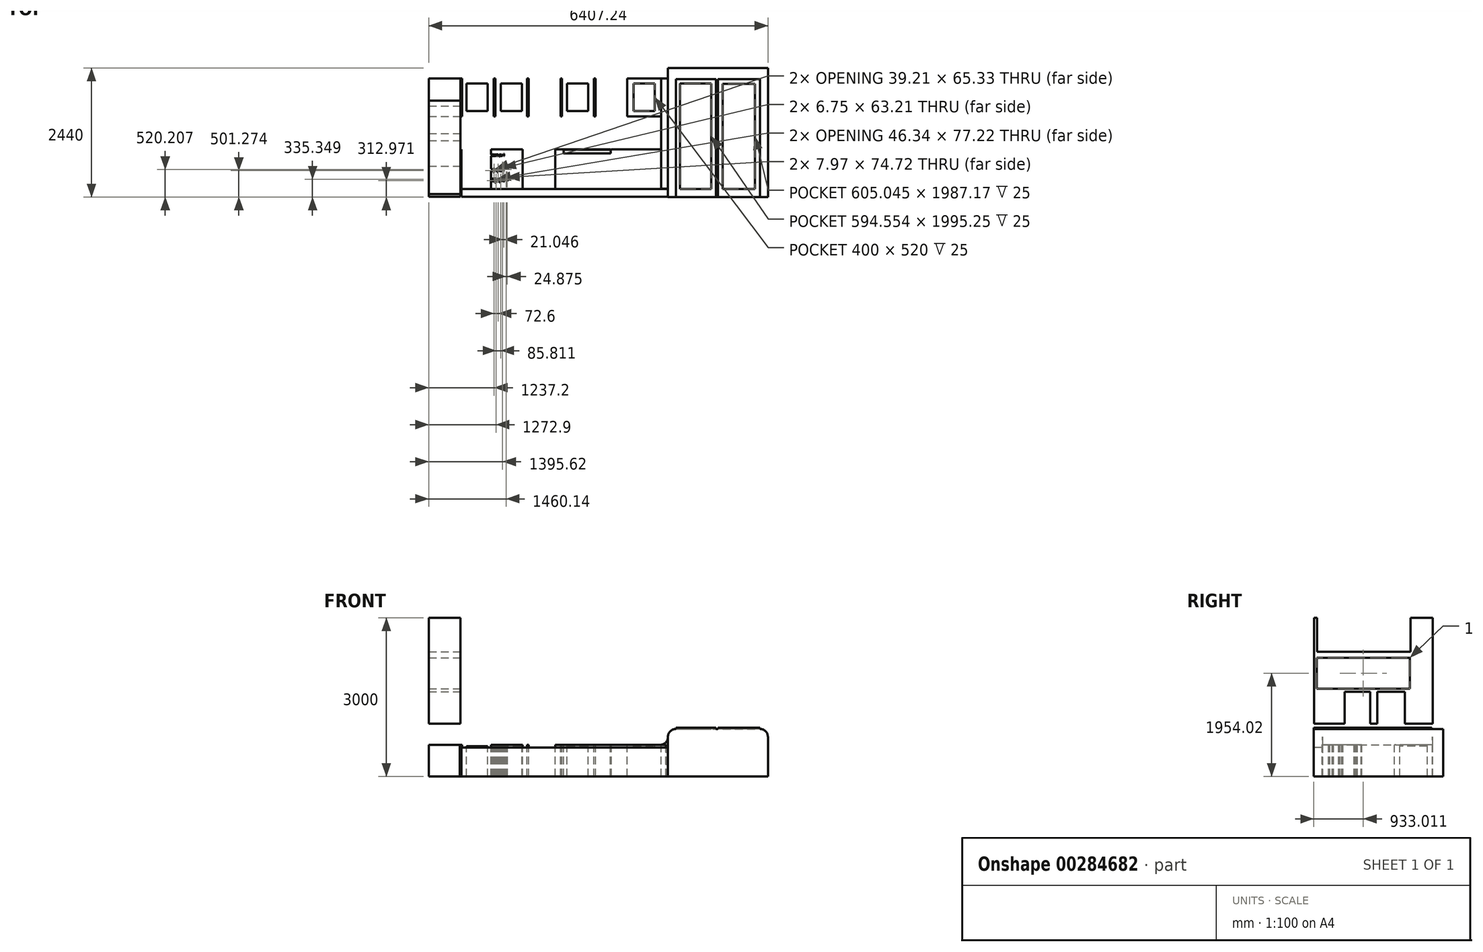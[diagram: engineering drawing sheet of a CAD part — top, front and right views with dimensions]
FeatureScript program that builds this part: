
annotation { "Feature Type Name" : "Feature", "Feature Type Description" : "" }
export const myFeature = defineFeature(function(context is Context, id is Id, definition is map)
    precondition{}
    {
        {
            var Q0;
            Q0=qCreatedBy(makeId("Top.planeOp"), FACE);
            var sketch = newSketch(context, id + "F0", { "sketchPlane" : qUnion([Q0])});
            skLineSegment(sketch, "E0.bottom", {"start": v(0, 750) * mm, "end": v(1806, 750) * mm});
            skLineSegment(sketch, "E0.top", {"start": v(0, 0) * mm, "end": v(3890, 0) * mm});
            skLineSegment(sketch, "E0.left", {"start": v(0, 750) * mm, "end": v(0, 0) * mm});
            skLineSegment(sketch, "E0.right", {"start": v(3890, 750) * mm, "end": v(3890, 0) * mm});
            skLineSegment(sketch, "E1.bottom", {"start": v(1190, 750) * mm, "end": v(1790, 750) * mm});
            skLineSegment(sketch, "E1.top", {"start": v(1190, 0) * mm, "end": v(1790, 0) * mm});
            skLineSegment(sketch, "E1.left", {"start": v(1190, 750) * mm, "end": v(1190, 0) * mm});
            skLineSegment(sketch, "E1.right", {"start": v(1790, 750) * mm, "end": v(1790, 0) * mm});
            skLineSegment(sketch, "E2.bottom", {"start": v(600, 740) * mm, "end": v(1164, 740) * mm});
            skLineSegment(sketch, "E2.top", {"start": v(600, 590) * mm, "end": v(1164, 590) * mm});
            skLineSegment(sketch, "E2.left", {"start": v(600, 740) * mm, "end": v(600, 590) * mm});
            skLineSegment(sketch, "E2.right", {"start": v(1164, 740) * mm, "end": v(1164, 590) * mm});
            skLineSegment(sketch, "E3.bottom", {"start": v(600, 560) * mm, "end": v(1164, 560) * mm});
            skLineSegment(sketch, "E3.top", {"start": v(600, 300) * mm, "end": v(1164, 300) * mm});
            skLineSegment(sketch, "E3.left", {"start": v(600, 560) * mm, "end": v(600, 300) * mm});
            skLineSegment(sketch, "E3.right", {"start": v(1164, 560) * mm, "end": v(1164, 300) * mm});
            skLineSegment(sketch, "E4.bottom", {"start": v(600, 270) * mm, "end": v(1164, 270) * mm});
            skLineSegment(sketch, "E4.top", {"start": v(600, 10) * mm, "end": v(1164, 10) * mm});
            skLineSegment(sketch, "E4.left", {"start": v(600, 270) * mm, "end": v(600, 10) * mm});
            skLineSegment(sketch, "E4.right", {"start": v(1164, 270) * mm, "end": v(1164, 10) * mm});
            skLineSegment(sketch, "E5.top", {"start": v(1816, 590) * mm, "end": v(2843, 590) * mm});
            skLineSegment(sketch, "E5.left", {"start": v(1816, 740) * mm, "end": v(1816, 590) * mm});
            skLineSegment(sketch, "E5.right", {"start": v(2843, 740) * mm, "end": v(2843, 590) * mm});
            skLineSegment(sketch, "E6.top", {"start": v(1816, 300) * mm, "end": v(2843, 300) * mm});
            skLineSegment(sketch, "E6.right", {"start": v(2843, 750) * mm, "end": v(2843, 590) * mm});
            skLineSegment(sketch, "E7.bottom", {"start": v(1826, 270) * mm, "end": v(2843, 270) * mm});
            skLineSegment(sketch, "E7.top", {"start": v(1826, 10) * mm, "end": v(2843, 10) * mm});
            skLineSegment(sketch, "E7.left", {"start": v(1826, 270) * mm, "end": v(1826, 10) * mm});
            skLineSegment(sketch, "E7.right", {"start": v(2843, 270) * mm, "end": v(2843, 10) * mm});
            skLineSegment(sketch, "E8.bottom", {"start": v(2853, 740) * mm, "end": v(3880, 740) * mm});
            skLineSegment(sketch, "E8.top", {"start": v(2853, 590) * mm, "end": v(3880, 590) * mm});
            skLineSegment(sketch, "E8.left", {"start": v(2853, 740) * mm, "end": v(2853, 590) * mm});
            skLineSegment(sketch, "E9.bottom", {"start": v(2853, 560) * mm, "end": v(3880, 560) * mm});
            skLineSegment(sketch, "E9.top", {"start": v(2853, 300) * mm, "end": v(3880, 300) * mm});
            skLineSegment(sketch, "E9.left", {"start": v(2853, 560) * mm, "end": v(2853, 300) * mm});
            skLineSegment(sketch, "E9.right", {"start": v(3880, 560) * mm, "end": v(3880, 300) * mm});
            skLineSegment(sketch, "E10.bottom", {"start": v(2853, 270) * mm, "end": v(3880, 270) * mm});
            skLineSegment(sketch, "E10.top", {"start": v(2853, 10) * mm, "end": v(3880, 10) * mm});
            skLineSegment(sketch, "E10.left", {"start": v(2853, 270) * mm, "end": v(2853, 10) * mm});
            skLineSegment(sketch, "E10.right", {"start": v(3880, 270) * mm, "end": v(3880, 10) * mm});
            skLineSegment(sketch, "E11.bottom", {"start": v(12.85, 1370) * mm, "end": v(3902.85, 1370) * mm});
            skLineSegment(sketch, "E11.top", {"start": v(12.85, 2090) * mm, "end": v(3902.85, 2090) * mm});
            skLineSegment(sketch, "E11.left", {"start": v(12.85, 1370) * mm, "end": v(12.85, 2090) * mm});
            skLineSegment(sketch, "E11.right", {"start": v(3902.85, 1370) * mm, "end": v(3902.85, 2090) * mm});
            skText(sketch, "E12", { "text": "Dishwasher", "fontName": "OpenSans-Regular.ttf"});
            skLineSegment(sketch, "E13", {"start": v(1174, 750) * mm, "end": v(1174, 0) * mm});
            skLineSegment(sketch, "E14", {"start": v(1806, 750) * mm, "end": v(1806, 0) * mm});
            skLineSegment(sketch, "E15", {"start": v(1816, 740) * mm, "end": v(2843, 740) * mm});
            skLineSegment(sketch, "E16", {"start": v(3890, 750) * mm, "end": v(1806, 750) * mm});
            skLineSegment(sketch, "E17", {"start": v(3880, 590) * mm, "end": v(3880, 740) * mm});
            skLineSegment(sketch, "E18", {"start": v(1816, 300) * mm, "end": v(1816, 560) * mm});
            skLineSegment(sketch, "E19", {"start": v(1816, 560) * mm, "end": v(2843, 560) * mm});
            skLineSegment(sketch, "E20.trimOffspring", {"start": v(2843, 560) * mm, "end": v(2843, 300) * mm});
            skLineSegment(sketch, "E21.bottom", {"start": v(42.85, 2090) * mm, "end": v(642.85, 2090) * mm});
            skLineSegment(sketch, "E21.top", {"start": v(42.85, 1370) * mm, "end": v(642.85, 1370) * mm});
            skLineSegment(sketch, "E21.left", {"start": v(42.85, 2090) * mm, "end": v(42.85, 1370) * mm});
            skLineSegment(sketch, "E21.right", {"start": v(642.85, 2090) * mm, "end": v(642.85, 1370) * mm});
            skLineSegment(sketch, "E22", {"start": v(6000, -150) * mm, "end": v(6000, 2090) * mm, "construction": true});
            skPoint(sketch, "E23", {"position": v(6000, 0) * mm});
            skPoint(sketch, "E24", {"position": v(6000, 1370) * mm});
            skPoint(sketch, "E25", {"position": v(6000, 750) * mm});
            skPoint(sketch, "E26", {"position": v(6000, 770) * mm});
            skLineSegment(sketch, "E27", {"start": v(6000, 2090) * mm, "end": v(5702.85, 2090) * mm, "construction": true});
            skLineSegment(sketch, "E28", {"start": v(6000, 2090) * mm, "end": v(6000, 2090) * mm});
            skLineSegment(sketch, "E29.bottom", {"start": v(672.85, 2090) * mm, "end": v(1272.85, 2090) * mm});
            skLineSegment(sketch, "E29.top", {"start": v(672.85, 1370) * mm, "end": v(1272.85, 1370) * mm});
            skLineSegment(sketch, "E29.left", {"start": v(672.85, 2090) * mm, "end": v(672.85, 1370) * mm});
            skLineSegment(sketch, "E29.right", {"start": v(1272.85, 2090) * mm, "end": v(1272.85, 1370) * mm});
            skLineSegment(sketch, "E30.bottom", {"start": v(1302.85, 2090) * mm, "end": v(1902.85, 2090) * mm});
            skLineSegment(sketch, "E30.top", {"start": v(1302.85, 1370) * mm, "end": v(1902.85, 1370) * mm});
            skLineSegment(sketch, "E30.left", {"start": v(1302.85, 2090) * mm, "end": v(1302.85, 1370) * mm});
            skLineSegment(sketch, "E30.right", {"start": v(1902.85, 2090) * mm, "end": v(1902.85, 1370) * mm});
            skLineSegment(sketch, "E31.bottom", {"start": v(1932.85, 2090) * mm, "end": v(2532.85, 2090) * mm});
            skLineSegment(sketch, "E31.top", {"start": v(1932.85, 1370) * mm, "end": v(2532.85, 1370) * mm});
            skLineSegment(sketch, "E31.left", {"start": v(1932.85, 2090) * mm, "end": v(1932.85, 1370) * mm});
            skLineSegment(sketch, "E31.right", {"start": v(2532.85, 2090) * mm, "end": v(2532.85, 1370) * mm});
            skLineSegment(sketch, "E32.bottom", {"start": v(2562.85, 2090) * mm, "end": v(3162.85, 2090) * mm});
            skLineSegment(sketch, "E32.top", {"start": v(2562.85, 1370) * mm, "end": v(3162.85, 1370) * mm});
            skLineSegment(sketch, "E32.left", {"start": v(2562.85, 2090) * mm, "end": v(2562.85, 1370) * mm});
            skLineSegment(sketch, "E32.right", {"start": v(3162.85, 2090) * mm, "end": v(3162.85, 1370) * mm});
            skLineSegment(sketch, "E33.bottom", {"start": v(3162.85, 2090) * mm, "end": v(3192.85, 2090) * mm});
            skLineSegment(sketch, "E33.top", {"start": v(3162.85, 1370) * mm, "end": v(3192.85, 1370) * mm});
            skLineSegment(sketch, "E33.left", {"start": v(3192.85, 2090) * mm, "end": v(3192.85, 1370) * mm});
            skLineSegment(sketch, "E34.bottom", {"start": v(3192.85, 2090) * mm, "end": v(3792.85, 2090) * mm});
            skLineSegment(sketch, "E34.top", {"start": v(3192.85, 1370) * mm, "end": v(3792.85, 1370) * mm});
            skLineSegment(sketch, "E34.right", {"start": v(3792.85, 2090) * mm, "end": v(3792.85, 1370) * mm});
            skLineSegment(sketch, "E35.bottom", {"start": v(30, 750) * mm, "end": v(590, 750) * mm});
            skLineSegment(sketch, "E35.top", {"start": v(30, 0) * mm, "end": v(590, 0) * mm});
            skLineSegment(sketch, "E35.left", {"start": v(30, 750) * mm, "end": v(30, 0) * mm});
            skLineSegment(sketch, "E35.right", {"start": v(590, 750) * mm, "end": v(590, 0) * mm});
            skText(sketch, "E36", { "text": "Lemans II \n541.32.620", "fontName": "OpenSans-Regular.ttf"});
            skText(sketch, "E37", { "text": "Bottom pull", "fontName": "OpenSans-Regular.ttf"});
            skText(sketch, "E38", { "text": "top pull", "fontName": "OpenSans-Regular.ttf"});
            skText(sketch, "E39", { "text": "top pull", "fontName": "OpenSans-Regular.ttf"});
            skLineSegment(sketch, "E40", {"start": v(6000, -150) * mm, "end": v(0, -150) * mm, "construction": true});
            skLineSegment(sketch, "E41.bottom", {"start": v(3902.85, 2090) * mm, "end": v(5702.85, 2090) * mm});
            skLineSegment(sketch, "E41.top", {"start": v(3902.85, 0) * mm, "end": v(5702.85, 0) * mm});
            skLineSegment(sketch, "E41.left", {"start": v(3902.85, 2090) * mm, "end": v(3902.85, 0) * mm});
            skLineSegment(sketch, "E41.right", {"start": v(5702.85, 2090) * mm, "end": v(5702.85, 0) * mm});
            skLineSegment(sketch, "E42", {"start": v(4772.85, 2090) * mm, "end": v(4772.85, 0) * mm});
            skLineSegment(sketch, "E43", {"start": v(4802.85, 2090) * mm, "end": v(4802.85, 0) * mm});
            skLineSegment(sketch, "E44", {"start": v(3932.85, 2090) * mm, "end": v(3932.85, 0) * mm});
            skLineSegment(sketch, "E45.bottom", {"start": v(127.34, 1990) * mm, "end": v(527.34, 1990) * mm});
            skLineSegment(sketch, "E45.top", {"start": v(127.34, 1470) * mm, "end": v(527.34, 1470) * mm});
            skLineSegment(sketch, "E45.left", {"start": v(127.34, 1990) * mm, "end": v(127.34, 1470) * mm});
            skLineSegment(sketch, "E45.right", {"start": v(527.34, 1990) * mm, "end": v(527.34, 1470) * mm});
            skLineSegment(sketch, "E46.bottom", {"start": v(772.85, 1990) * mm, "end": v(1172.85, 1990) * mm});
            skLineSegment(sketch, "E46.top", {"start": v(772.85, 1470) * mm, "end": v(1172.85, 1470) * mm});
            skLineSegment(sketch, "E46.left", {"start": v(772.85, 1990) * mm, "end": v(772.85, 1470) * mm});
            skLineSegment(sketch, "E46.right", {"start": v(1172.85, 1990) * mm, "end": v(1172.85, 1470) * mm});
            skLineSegment(sketch, "E47.bottom", {"start": v(2028.05, 1990) * mm, "end": v(2428.05, 1990) * mm});
            skLineSegment(sketch, "E47.top", {"start": v(2028.05, 1470) * mm, "end": v(2428.05, 1470) * mm});
            skLineSegment(sketch, "E47.left", {"start": v(2028.05, 1990) * mm, "end": v(2028.05, 1470) * mm});
            skLineSegment(sketch, "E47.right", {"start": v(2428.05, 1990) * mm, "end": v(2428.05, 1470) * mm});
            skLineSegment(sketch, "E48.bottom", {"start": v(3280.66, 1990) * mm, "end": v(3680.66, 1990) * mm});
            skLineSegment(sketch, "E48.top", {"start": v(3280.66, 1470) * mm, "end": v(3680.66, 1470) * mm});
            skLineSegment(sketch, "E48.left", {"start": v(3280.66, 1990) * mm, "end": v(3280.66, 1470) * mm});
            skLineSegment(sketch, "E48.right", {"start": v(3680.66, 1990) * mm, "end": v(3680.66, 1470) * mm});
            skText(sketch, "E49", { "text": "Stove", "fontName": "OpenSans-Regular.ttf"});
            skPoint(sketch, "E50", {"position": v(2061.13, 1179.17) * mm});
            skPoint(sketch, "E51", {"position": v(2414.2, 750) * mm});
            skLineSegment(sketch, "E52.bottom", {"start": v(1964.2, 750) * mm, "end": v(2864.2, 750) * mm});
            skLineSegment(sketch, "E52.top", {"start": v(1964.2, 670) * mm, "end": v(2864.2, 670) * mm});
            skLineSegment(sketch, "E52.left", {"start": v(1964.2, 750) * mm, "end": v(1964.2, 670) * mm});
            skLineSegment(sketch, "E52.right", {"start": v(2864.2, 750) * mm, "end": v(2864.2, 670) * mm});
            skLineSegment(sketch, "E53.bottom", {"start": v(3932.85, 2090) * mm, "end": v(4091.6, 2090) * mm});
            skLineSegment(sketch, "E53.top", {"start": v(3932.85, -150) * mm, "end": v(4091.6, -150) * mm});
            skLineSegment(sketch, "E53.left", {"start": v(3932.85, 2090) * mm, "end": v(3932.85, -150) * mm});
            skLineSegment(sketch, "E53.right", {"start": v(4091.6, 2090) * mm, "end": v(4091.6, -150) * mm});
            skLineSegment(sketch, "E54.bottom", {"start": v(5586.52, 2090) * mm, "end": v(5820.09, 2090) * mm});
            skLineSegment(sketch, "E54.top", {"start": v(5586.52, -159.02) * mm, "end": v(5820.09, -159.02) * mm});
            skLineSegment(sketch, "E54.left", {"start": v(5586.52, 2090) * mm, "end": v(5586.52, -159.02) * mm});
            skLineSegment(sketch, "E54.right", {"start": v(5820.09, 2090) * mm, "end": v(5820.09, -159.02) * mm});
            skPoint(sketch, "E55.oppositeSnap0", {"position": v(5703.3, 2090) * mm});
            skLineSegment(sketch, "E55.bottom", {"start": v(3932.85, 2286.83) * mm, "end": v(5820.09, 2286.83) * mm});
            skLineSegment(sketch, "E55.top", {"start": v(3932.85, 2090) * mm, "end": v(5820.09, 2090) * mm});
            skLineSegment(sketch, "E55.left", {"start": v(3932.85, 2286.83) * mm, "end": v(3932.85, 2090) * mm});
            skLineSegment(sketch, "E55.right", {"start": v(5820.09, 2286.83) * mm, "end": v(5820.09, 2090) * mm});
            skLineSegment(sketch, "E56.trimOffspring", {"start": v(3932.85, 2090) * mm, "end": v(12.85, 2090) * mm, "construction": true});
            skLineSegment(sketch, "E57.trimOffspring", {"start": v(5586.52, 2090) * mm, "end": v(4091.6, 2090) * mm, "construction": true});
            skLineSegment(sketch, "E58.bottom", {"start": v(1405.73, 1990) * mm, "end": v(1817.16, 1990) * mm});
            skLineSegment(sketch, "E58.top", {"start": v(1405.73, 1470) * mm, "end": v(1817.16, 1470) * mm});
            skLineSegment(sketch, "E58.left", {"start": v(1405.73, 1990) * mm, "end": v(1405.73, 1470) * mm});
            skLineSegment(sketch, "E58.right", {"start": v(1817.16, 1990) * mm, "end": v(1817.16, 1470) * mm});
            skLineSegment(sketch, "E59.bottom", {"start": v(2646, 1990) * mm, "end": v(3066.6, 1990) * mm});
            skLineSegment(sketch, "E59.top", {"start": v(2646, 1470) * mm, "end": v(3066.6, 1470) * mm});
            skLineSegment(sketch, "E59.left", {"start": v(2646, 1990) * mm, "end": v(2646, 1470) * mm});
            skLineSegment(sketch, "E59.right", {"start": v(3066.6, 1990) * mm, "end": v(3066.6, 1470) * mm});
            skLineSegment(sketch, "E60.bottom", {"start": v(30, 0) * mm, "end": v(0, 0) * mm});
            skLineSegment(sketch, "E60.top", {"start": v(30, -150) * mm, "end": v(0, -150) * mm});
            skLineSegment(sketch, "E60.left", {"start": v(30, 0) * mm, "end": v(30, -150) * mm});
            skLineSegment(sketch, "E60.right", {"start": v(0, 0) * mm, "end": v(0, -150) * mm});
            skLineSegment(sketch, "E61.bottom", {"start": v(0, 0) * mm, "end": v(3932.85, 0) * mm});
            skLineSegment(sketch, "E61.top", {"start": v(0, -150) * mm, "end": v(3932.85, -150) * mm});
            skLineSegment(sketch, "E61.right", {"start": v(3932.85, 0) * mm, "end": v(3932.85, -150) * mm});
            skLineSegment(sketch, "E62.bottom", {"start": v(4091.6, 0) * mm, "end": v(5586.52, 0) * mm});
            skLineSegment(sketch, "E62.top", {"start": v(4091.6, -159.02) * mm, "end": v(5586.52, -159.02) * mm});
            skLineSegment(sketch, "E62.left", {"start": v(4091.6, 0) * mm, "end": v(4091.6, -159.02) * mm});
            skLineSegment(sketch, "E62.right", {"start": v(5586.52, 0) * mm, "end": v(5586.52, -159.02) * mm});
            const initialGuessF0  = {"E12": [1.29, 0.4978, 1, 0, 0.0522], "E36": [0.08, 0.61298, 1, 0, 0.04765], "E37": [0.54096, 0.62134, 1, 0, 0.03929], "E38": [0.54368, 0.33543, 1, 0, 0.0599], "E39": [0.56002, 0.14482, 1, 0, 0.0708], "E49": [1.91777, 1.09917, 1, 0, 0.08]};
            skSetInitialGuess(sketch, initialGuessF0);
            skSolve(sketch);
        }
        {
            var Q0;
            {var subQ0=sQuery(id+"F0.wireOp",EDGE,"E11.left");Q0=makeQuery(id+"F0.imprint","IMPRINT",FACE,{"disambiguationData":[TD([[makeQuery(id+"F0.imprint","IMPRINT",EDGE,{"derivedFrom":subQ0}),-1.0]])]});}
            var Q1;
            Q1=makeQuery(id+"F0.imprint","IMPRINT",FACE,{"disambiguationData":[TD([[makeQuery(id+"F0.imprint","IMPRINT",EDGE,{"derivedFrom":sQuery(id+"F0.wireOp",EDGE,"E21.bottom")}),-1.0]])]});
            var Q2;
            {var subQ0=sQuery(id+"F0.wireOp",EDGE,"E21.right");Q2=makeQuery(id+"F0.imprint","IMPRINT",FACE,{"disambiguationData":[TD([[makeQuery(id+"F0.imprint","IMPRINT",EDGE,{"derivedFrom":subQ0}),1.0]])]});}
            var Q3;
            Q3=makeQuery(id+"F0.imprint","IMPRINT",FACE,{"disambiguationData":[TD([[makeQuery(id+"F0.imprint","IMPRINT",EDGE,{"derivedFrom":sQuery(id+"F0.wireOp",EDGE,"E29.bottom")}),-1.0]])]});
            var Q4;
            Q4=makeQuery(id+"F0.imprint","IMPRINT",FACE,{"disambiguationData":[TD([[makeQuery(id+"F0.imprint","IMPRINT",EDGE,{"derivedFrom":sQuery(id+"F0.wireOp",EDGE,"E30.bottom")}),-1.0]])]});
            var Q5;
            Q5=makeQuery(id+"F0.imprint","IMPRINT",FACE,{"disambiguationData":[TD([[makeQuery(id+"F0.imprint","IMPRINT",EDGE,{"derivedFrom":sQuery(id+"F0.wireOp",EDGE,"E32.bottom")}),-1.0]])]});
            var Q6;
            {var subQ0=sQuery(id+"F0.wireOp",EDGE,"E31.right");Q6=makeQuery(id+"F0.imprint","IMPRINT",FACE,{"disambiguationData":[TD([[makeQuery(id+"F0.imprint","IMPRINT",EDGE,{"derivedFrom":subQ0}),1.0]])]});}
            var Q7;
            Q7=makeQuery(id+"F0.imprint","IMPRINT",FACE,{"disambiguationData":[TD([[makeQuery(id+"F0.imprint","IMPRINT",EDGE,{"derivedFrom":sQuery(id+"F0.wireOp",EDGE,"E32.right")}),1.0]])]});
            var Q8;
            Q8=makeQuery(id+"F0.imprint","IMPRINT",FACE,{"disambiguationData":[TD([[makeQuery(id+"F0.imprint","IMPRINT",EDGE,{"derivedFrom":sQuery(id+"F0.wireOp",EDGE,"E33.left")}),1.0]])]});
            var Q9;
            Q9=makeQuery(id+"F0.imprint","IMPRINT",FACE,{"disambiguationData":[TD([[makeQuery(id+"F0.imprint","IMPRINT",EDGE,{"derivedFrom":sQuery(id+"F0.wireOp",EDGE,"E48.bottom")}),-1.0]])]});
            var Q10;
            {var subQ3=sQuery(id+"F0.wireOp",EDGE,"E34.right");Q10=makeQuery(id+"F0.imprint","IMPRINT",FACE,{"disambiguationData":[TD([[makeQuery(id+"F0.imprint","IMPRINT",EDGE,{"derivedFrom":subQ3}),1.0]])]});}
            var Q11;
            {var subQ4=sQuery(id+"F0.wireOp",EDGE,"E41.bottom");Q11=makeQuery(id+"F0.imprint","IMPRINT",FACE,{"disambiguationData":[TD([[makeQuery(id+"F0.imprint","IMPRINT",EDGE,{"derivedFrom":subQ4}),-1.0]])]});}
            var Q12;
            {var subQ0=sQuery(id+"F0.wireOp",EDGE,"E53.left");var subQ1=sQuery(id+"F0.wireOp",EDGE,"E41.top");var subQ2=makeQuery(id+"F0.imprint","INTERSECT",VERTEX,{"derivedFrom":[subQ1,subQ0]});Q12=makeQuery(id+"F0.imprint","IMPRINT",FACE,{"disambiguationData":[TD([[makeQuery(id+"F0.imprint","IMPRINT",EDGE,{"disambiguationData":[TD([[subQ2,-1.0]])],"derivedFrom":subQ1}),1.0]])]});}
            var Q13;
            Q13=makeQuery(id+"F0.imprint","IMPRINT",FACE,{"disambiguationData":[TD([[makeQuery(id+"F0.imprint","IMPRINT",EDGE,{"derivedFrom":sQuery(id+"F0.wireOp",EDGE,"E55.bottom")}),-1.0]])]});
            var Q14;
            {var subQ0=sQuery(id+"F0.wireOp",EDGE,"E42");Q14=makeQuery(id+"F0.imprint","IMPRINT",FACE,{"disambiguationData":[TD([[makeQuery(id+"F0.imprint","IMPRINT",EDGE,{"derivedFrom":subQ0}),-1.0]])]});}
            var Q15;
            {var subQ0=sQuery(id+"F0.wireOp",EDGE,"E42");Q15=makeQuery(id+"F0.imprint","IMPRINT",FACE,{"disambiguationData":[TD([[makeQuery(id+"F0.imprint","IMPRINT",EDGE,{"derivedFrom":subQ0}),1.0]])]});}
            var Q16;
            Q16=makeQuery(id+"F0.imprint","IMPRINT",FACE,{"disambiguationData":[TD([[makeQuery(id+"F0.imprint","IMPRINT",EDGE,{"derivedFrom":sQuery(id+"F0.wireOp",EDGE,"E1.bottom")}),-1.0]])]});
            var Q17;
            {var subQ7=sQuery(id+"F0.wireOp",EDGE,"E5.top");Q17=makeQuery(id+"F0.imprint","IMPRINT",FACE,{"disambiguationData":[TD([[makeQuery(id+"F0.imprint","IMPRINT",EDGE,{"derivedFrom":subQ7}),1.0]])]});}
            var Q18;
            {var subQ0=sQuery(id+"F0.wireOp",EDGE,"E42");Q18=makeQuery(id+"F0.imprint","IMPRINT",FACE,{"disambiguationData":[TD([[makeQuery(id+"F0.imprint","IMPRINT",EDGE,{"derivedFrom":subQ0}),-1.0]])]});}
            var Q19;
            {var subQ0=sQuery(id+"F0.wireOp",EDGE,"E41.right");Q19=makeQuery(id+"F0.imprint","IMPRINT",FACE,{"disambiguationData":[TD([[makeQuery(id+"F0.imprint","IMPRINT",EDGE,{"derivedFrom":subQ0}),-1.0]])]});}
            var Q20;
            {var subQ0=sQuery(id+"F0.wireOp",EDGE,"E43");Q20=makeQuery(id+"F0.imprint","IMPRINT",FACE,{"disambiguationData":[TD([[makeQuery(id+"F0.imprint","IMPRINT",EDGE,{"derivedFrom":subQ0}),1.0]])]});}
            var Q21;
            {var subQ4=sQuery(id+"F0.wireOp",EDGE,"E41.right");Q21=makeQuery(id+"F0.imprint","IMPRINT",FACE,{"disambiguationData":[TD([[makeQuery(id+"F0.imprint","IMPRINT",EDGE,{"derivedFrom":subQ4}),1.0]])]});}
            var Q22;
            {var subQ1=sQuery(id+"F0.wireOp",EDGE,"E8.top");Q22=makeQuery(id+"F0.imprint","IMPRINT",FACE,{"disambiguationData":[TD([[makeQuery(id+"F0.imprint","IMPRINT",EDGE,{"derivedFrom":subQ1}),1.0]])]});}
            var Q23;
            Q23=makeQuery(id+"F0.imprint","IMPRINT",FACE,{"disambiguationData":[TD([[makeQuery(id+"F0.imprint","IMPRINT",EDGE,{"derivedFrom":sQuery(id+"F0.wireOp",EDGE,"E9.bottom")}),-1.0]])]});
            var Q24;
            Q24=makeQuery(id+"F0.imprint","IMPRINT",FACE,{"disambiguationData":[TD([[makeQuery(id+"F0.imprint","IMPRINT",EDGE,{"derivedFrom":sQuery(id+"F0.wireOp",EDGE,"E10.bottom")}),-1.0]])]});
            var Q25;
            Q25=makeQuery(id+"F0.imprint","IMPRINT",FACE,{"disambiguationData":[TD([[makeQuery(id+"F0.imprint","IMPRINT",EDGE,{"derivedFrom":sQuery(id+"F0.wireOp",EDGE,"E7.bottom")}),-1.0]])]});
            var Q26;
            Q26=makeQuery(id+"F0.imprint","IMPRINT",FACE,{"disambiguationData":[TD([[makeQuery(id+"F0.imprint","IMPRINT",EDGE,{"derivedFrom":sQuery(id+"F0.wireOp",EDGE,"E6.top")}),1.0]])]});
            var Q27;
            {var subQ0=sQuery(id+"F0.wireOp",EDGE,"E15");var subQ1=sQuery(id+"F0.wireOp",EDGE,"E6.right");var subQ2=makeQuery(id+"F0.imprint","INTERSECT",VERTEX,{"derivedFrom":[subQ1,subQ0]});Q27=makeQuery(id+"F0.imprint","IMPRINT",FACE,{"disambiguationData":[TD([[makeQuery(id+"F0.imprint","IMPRINT",EDGE,{"disambiguationData":[TD([[subQ2,-1.0]])],"derivedFrom":subQ1}),-1.0]])]});}
            var Q28;
            {var subQ7=sQuery(id+"F0.wireOp",EDGE,"E3.bottom");Q28=makeQuery(id+"F0.imprint","IMPRINT",FACE,{"disambiguationData":[TD([[makeQuery(id+"F0.imprint","IMPRINT",EDGE,{"derivedFrom":subQ7}),-1.0]])]});}
            var Q29;
            {var subQ8=sQuery(id+"F0.wireOp",EDGE,"E2.bottom");Q29=makeQuery(id+"F0.imprint","IMPRINT",FACE,{"disambiguationData":[TD([[makeQuery(id+"F0.imprint","IMPRINT",EDGE,{"derivedFrom":subQ8}),-1.0]])]});}
            var Q30;
            Q30=makeQuery(id+"F0.imprint","IMPRINT",FACE,{"disambiguationData":[TD([[makeQuery(id+"F0.imprint","IMPRINT",EDGE,{"derivedFrom":sQuery(id+"F0.wireOp",EDGE,"E4.bottom")}),-1.0]])]});
            var Q31;
            {var subQ14=sQuery(id+"F0.wireOp",EDGE,"E35.bottom");Q31=makeQuery(id+"F0.imprint","IMPRINT",FACE,{"disambiguationData":[TD([[makeQuery(id+"F0.imprint","IMPRINT",EDGE,{"derivedFrom":subQ14}),-1.0]])]});}
            var Q32;
            {var subQ0=sQuery(id+"F0.wireOp",EDGE,"E0.left");Q32=makeQuery(id+"F0.imprint","IMPRINT",FACE,{"disambiguationData":[TD([[makeQuery(id+"F0.imprint","IMPRINT",EDGE,{"derivedFrom":subQ0}),1.0]])]});}
            var Q33;
            Q33=makeQuery(id+"F0.imprint","IMPRINT",FACE,{"disambiguationData":[TD([[makeQuery(id+"F0.imprint","IMPRINT",EDGE,{"derivedFrom":sQuery(id+"F0.wireOp",EDGE,"E45.bottom")}),-1.0]])]});
            var Q34;
            Q34=makeQuery(id+"F0.imprint","IMPRINT",FACE,{"disambiguationData":[TD([[makeQuery(id+"F0.imprint","IMPRINT",EDGE,{"derivedFrom":sQuery(id+"F0.wireOp",EDGE,"E46.bottom")}),-1.0]])]});
            var Q35;
            Q35=makeQuery(id+"F0.imprint","IMPRINT",FACE,{"disambiguationData":[TD([[makeQuery(id+"F0.imprint","IMPRINT",EDGE,{"derivedFrom":sQuery(id+"F0.wireOp",EDGE,"E31.bottom")}),-1.0]])]});
            var Q36;
            Q36=makeQuery(id+"F0.imprint","IMPRINT",FACE,{"disambiguationData":[TD([[makeQuery(id+"F0.imprint","IMPRINT",EDGE,{"derivedFrom":sQuery(id+"F0.wireOp",EDGE,"E47.bottom")}),-1.0]])]});
            var Q37;
            {var subQ5=sQuery(id+"F0.wireOp",EDGE,"E53.top");Q37=makeQuery(id+"F0.imprint","IMPRINT",FACE,{"disambiguationData":[TD([[makeQuery(id+"F0.imprint","IMPRINT",EDGE,{"derivedFrom":subQ5}),1.0]])]});}
            var Q38;
            {var subQ0=sQuery(id+"F0.wireOp",EDGE,"E29.right");Q38=makeQuery(id+"F0.imprint","IMPRINT",FACE,{"disambiguationData":[TD([[makeQuery(id+"F0.imprint","IMPRINT",EDGE,{"derivedFrom":subQ0}),1.0]])]});}
            var Q39;
            {var subQ0=sQuery(id+"F0.wireOp",EDGE,"E30.right");Q39=makeQuery(id+"F0.imprint","IMPRINT",FACE,{"disambiguationData":[TD([[makeQuery(id+"F0.imprint","IMPRINT",EDGE,{"derivedFrom":subQ0}),1.0]])]});}
            var Q40;
            {var subQ0=sQuery(id+"F0.wireOp",EDGE,"E0.right");Q40=makeQuery(id+"F0.imprint","IMPRINT",FACE,{"disambiguationData":[TD([[makeQuery(id+"F0.imprint","IMPRINT",EDGE,{"derivedFrom":subQ0}),-1.0]])]});}
            var Q41;
            {var subQ0=sQuery(id+"F0.wireOp",EDGE,"E8.left");var subQ1=sQuery(id+"F0.wireOp",EDGE,"E8.bottom");var subQ2=makeQuery(id+"F0.imprint","INTERSECT",VERTEX,{"derivedFrom":[subQ1,subQ0]});Q41=makeQuery(id+"F0.imprint","IMPRINT",FACE,{"disambiguationData":[TD([[makeQuery(id+"F0.imprint","IMPRINT",EDGE,{"disambiguationData":[TD([[subQ2,-1.0]])],"derivedFrom":subQ1}),-1.0]])]});}
            var Q42;
            {var subQ0=sQuery(id+"F0.wireOp",EDGE,"E1.left");Q42=makeQuery(id+"F0.imprint","IMPRINT",FACE,{"disambiguationData":[TD([[makeQuery(id+"F0.imprint","IMPRINT",EDGE,{"derivedFrom":subQ0}),-1.0]])]});}
            var Q43;
            {var subQ30=sQuery(id+"F0.wireOp",EDGE,"E2.bottom");Q43=makeQuery(id+"F0.imprint","IMPRINT",FACE,{"disambiguationData":[TD([[makeQuery(id+"F0.imprint","IMPRINT",EDGE,{"derivedFrom":subQ30}),1.0]])]});}
            extrude(context, id + "F1", {"entities" : qUnion([Q0, Q1, Q2, Q3, Q4, Q5, Q6, Q7, Q8, Q9, Q10, Q11, Q12, Q13, Q14, Q15, Q16, Q17, Q18, Q19, Q20, Q21, Q22, Q23, Q24, Q25, Q26, Q27, Q28, Q29, Q30, Q31, Q32, Q33, Q34, Q35, Q36, Q37, Q38, Q39, Q40, Q41, Q42, Q43]), "oppositeDirection" : true, "depth" : 600 * mm});
        }
        {
            var Q0;
            Q0=makeQuery(id+"F1.opExtrude","SWEPT_FACE",FACE,{"disambiguationData":[OSD([sQuery(id+"F0.wireOp",EDGE,"E55.bottom")])]});
            var sketch = newSketch(context, id + "F2", { "sketchPlane" : qUnion([Q0])});
            skLineSegment(sketch, "E63.bottom", {"start": v(-3932.85, -600) * mm, "end": v(-5820.09, -600) * mm});
            skLineSegment(sketch, "E63.top", {"start": v(-4082.85, 300) * mm, "end": v(-5670.09, 300) * mm});
            skLineSegment(sketch, "E63.left", {"start": v(-3932.85, 150) * mm, "end": v(-3932.85, 150) * mm});
            skLineSegment(sketch, "E63.right", {"start": v(-5820.09, -600) * mm, "end": v(-5820.09, 150) * mm});
            skPoint(sketch, "E64.visualSharp", {"position": v(-3932.85, 300) * mm});
            skArc(sketch, "E64.filletArc", {"start": v(-3932.85, 150) * mm, "mid": v(-3976.78, 256.07) * mm, "end": v(-4082.85, 300) * mm});
            skPoint(sketch, "E65.visualSharp", {"position": v(-5820.09, 300) * mm});
            skArc(sketch, "E65.filletArc", {"start": v(-5670.09, 300) * mm, "mid": v(-5776.15, 256.07) * mm, "end": v(-5820.09, 150) * mm});
            skPoint(sketch, "E66.visualSharp", {"position": v(-3932.85, 0) * mm});
            skLineSegment(sketch, "E67.bottom", {"start": v(-3932.85, -600) * mm, "end": v(-3803.33, -600) * mm});
            skLineSegment(sketch, "E67.left", {"start": v(-3932.85, -600) * mm, "end": v(-3932.85, 150) * mm});
            skLineSegment(sketch, "E67.right", {"start": v(-3803.33, -600) * mm, "end": v(-3803.33, 1.4) * mm});
            skLineSegment(sketch, "E68", {"start": v(-3782.85, 0) * mm, "end": v(-3782.85, 0) * mm});
            skArc(sketch, "E69.filletArc", {"start": v(-3932.85, 150) * mm, "mid": v(-3895.92, 51.44) * mm, "end": v(-3803.33, 1.4) * mm});
            skPoint(sketch, "E67.top.end.orphan", {"position": v(-3803.33, 150) * mm});
            skPoint(sketch, "E70.bottom.start.orphan", {"position": v(-3766.85, 0) * mm});
            skSolve(sketch);
        }
        {
            var Q0;
            Q0=makeQuery(id+"F2.imprint","IMPRINT",FACE,{"disambiguationData":[TD([[makeQuery(id+"F2.imprint","IMPRINT",EDGE,{"derivedFrom":sQuery(id+"F2.wireOp",EDGE,"E63.top")}),1.0]])]});
            var Q1;
            {var subQ0=sQuery(id+"F2.wireOp",EDGE,"E63.bottom");Q1=makeQuery(id+"F2.imprint","IMPRINT",FACE,{"disambiguationData":[TD([[makeQuery(id+"F2.imprint","IMPRINT",EDGE,{"derivedFrom":subQ0}),-1.0]])]});}
            extrude(context, id + "F3", {"entities" : qUnion([Q0, Q1]), "operationType" : NewBodyOperationType.ADD, "oppositeDirection" : true, "depth" : 2440 * mm});
        }
        {
            var Q0;
            Q0=makeQuery(id+"F3.opExtrude","SWEPT_FACE",FACE,{"disambiguationData":[OSD([sQuery(id+"F2.wireOp",EDGE,"E63.top")])]});
            var sketch = newSketch(context, id + "F4", { "sketchPlane" : qUnion([Q0])});
            skLineSegment(sketch, "E71.bottom", {"start": v(4082.85, 2073.08) * mm, "end": v(4839.76, 2073.08) * mm});
            skLineSegment(sketch, "E71.top", {"start": v(4082.85, -153.17) * mm, "end": v(4839.76, -153.17) * mm});
            skLineSegment(sketch, "E71.left", {"start": v(4082.85, 2073.08) * mm, "end": v(4082.85, -153.17) * mm});
            skLineSegment(sketch, "E71.right", {"start": v(4839.76, 2073.08) * mm, "end": v(4839.76, -153.17) * mm});
            skLineSegment(sketch, "E72.bottom", {"start": v(5670.09, 2074.07) * mm, "end": v(4876.47, 2074.07) * mm});
            skLineSegment(sketch, "E72.top", {"start": v(5670.09, -153.17) * mm, "end": v(4876.47, -153.17) * mm});
            skLineSegment(sketch, "E72.left", {"start": v(5670.09, 2074.07) * mm, "end": v(5670.09, -153.17) * mm});
            skLineSegment(sketch, "E72.right", {"start": v(4876.47, 2074.07) * mm, "end": v(4876.47, -153.17) * mm});
            skLineSegment(sketch, "E73.bottom", {"start": v(4157.12, 1995.25) * mm, "end": v(4751.68, 1995.25) * mm});
            skLineSegment(sketch, "E73.top", {"start": v(4157.12, 0) * mm, "end": v(4751.68, 0) * mm});
            skLineSegment(sketch, "E73.left", {"start": v(4157.12, 1995.25) * mm, "end": v(4157.12, 0) * mm});
            skLineSegment(sketch, "E73.right", {"start": v(4751.68, 1995.25) * mm, "end": v(4751.68, 0) * mm});
            skLineSegment(sketch, "E74.bottom", {"start": v(4967.17, 1987.17) * mm, "end": v(5572.21, 1987.17) * mm});
            skLineSegment(sketch, "E74.top", {"start": v(4967.17, 0) * mm, "end": v(5572.21, 0) * mm});
            skLineSegment(sketch, "E74.left", {"start": v(4967.17, 1987.17) * mm, "end": v(4967.17, 0) * mm});
            skLineSegment(sketch, "E74.right", {"start": v(5572.21, 1987.17) * mm, "end": v(5572.21, 0) * mm});
            skSolve(sketch);
        }
        {
            var Q0;
            Q0=makeQuery(id+"F4.imprint","IMPRINT",FACE,{"disambiguationData":[TD([[makeQuery(id+"F4.imprint","IMPRINT",EDGE,{"derivedFrom":sQuery(id+"F4.wireOp",EDGE,"E71.bottom")}),-1.0]])]});
            var Q1;
            Q1=makeQuery(id+"F4.imprint","IMPRINT",FACE,{"disambiguationData":[TD([[makeQuery(id+"F4.imprint","IMPRINT",EDGE,{"derivedFrom":sQuery(id+"F4.wireOp",EDGE,"E72.bottom")}),1.0]])]});
            extrude(context, id + "F5", {"entities" : qUnion([Q0, Q1]), "operationType" : NewBodyOperationType.ADD, "depth" : 25 * mm});
        }
        {
            var Q0;
            {var subQ5=sQuery(id+"F2.wireOp",EDGE,"E67.bottom");Q0=makeQuery(id+"F2.imprint","IMPRINT",FACE,{"disambiguationData":[TD([[makeQuery(id+"F2.imprint","IMPRINT",EDGE,{"derivedFrom":subQ5}),1.0]])]});}
            extrude(context, id + "F6", {"entities" : qUnion([Q0]), "operationType" : NewBodyOperationType.ADD, "oppositeDirection" : true, "depth" : 2280 * mm, "hasSecondDirection" : true, "secondDirectionOppositeDirection" : true, "secondDirectionDepth" : 200 * mm});
        }
        {
            var Q0;
            Q0=makeQuery(id+"F0.imprint","IMPRINT",FACE,{"disambiguationData":[TD([[makeQuery(id+"F0.imprint","IMPRINT",EDGE,{"derivedFrom":sQuery(id+"F0.wireOp",EDGE,"E45.bottom")}),-1.0]])]});
            var Q1;
            Q1=makeQuery(id+"F0.imprint","IMPRINT",FACE,{"disambiguationData":[TD([[makeQuery(id+"F0.imprint","IMPRINT",EDGE,{"derivedFrom":sQuery(id+"F0.wireOp",EDGE,"E46.bottom")}),-1.0]])]});
            var Q2;
            Q2=makeQuery(id+"F0.imprint","IMPRINT",FACE,{"disambiguationData":[TD([[makeQuery(id+"F0.imprint","IMPRINT",EDGE,{"derivedFrom":sQuery(id+"F0.wireOp",EDGE,"E47.bottom")}),-1.0]])]});
            var Q3;
            Q3=makeQuery(id+"F0.imprint","IMPRINT",FACE,{"disambiguationData":[TD([[makeQuery(id+"F0.imprint","IMPRINT",EDGE,{"derivedFrom":sQuery(id+"F0.wireOp",EDGE,"E48.bottom")}),-1.0]])]});
            extrude(context, id + "F7", {"entities" : qUnion([Q0, Q1, Q2, Q3]), "operationType" : NewBodyOperationType.ADD, "oppositeDirection" : true, "depth" : 25 * mm});
        }
        {
            var Q0;
            Q0=makeQuery(id+"F0.imprint","IMPRINT",FACE,{"disambiguationData":[TD([[makeQuery(id+"F0.imprint","IMPRINT",EDGE,{"derivedFrom":sQuery(id+"F0.wireOp",EDGE,"E45.bottom")}),-1.0]])]});
            var Q1;
            Q1=makeQuery(id+"F0.imprint","IMPRINT",FACE,{"disambiguationData":[TD([[makeQuery(id+"F0.imprint","IMPRINT",EDGE,{"derivedFrom":sQuery(id+"F0.wireOp",EDGE,"E46.bottom")}),-1.0]])]});
            var Q2;
            Q2=makeQuery(id+"F0.imprint","IMPRINT",FACE,{"disambiguationData":[TD([[makeQuery(id+"F0.imprint","IMPRINT",EDGE,{"derivedFrom":sQuery(id+"F0.wireOp",EDGE,"E47.bottom")}),-1.0]])]});
            var Q3;
            Q3=makeQuery(id+"F0.imprint","IMPRINT",FACE,{"disambiguationData":[TD([[makeQuery(id+"F0.imprint","IMPRINT",EDGE,{"derivedFrom":sQuery(id+"F0.wireOp",EDGE,"E48.bottom")}),-1.0]])]});
            extrude(context, id + "F8", {"entities" : qUnion([Q0, Q1, Q2, Q3]), "operationType" : NewBodyOperationType.REMOVE, "oppositeDirection" : true, "depth" : 25 * mm});
        }
        {
            var Q0;
            {var subQ8=sQuery(id+"F0.wireOp",EDGE,"E60.left");Q0=makeQuery(id+"F0.imprint","IMPRINT",FACE,{"disambiguationData":[TD([[makeQuery(id+"F0.imprint","IMPRINT",EDGE,{"derivedFrom":subQ8}),1.0]])]});}
            extrude(context, id + "F9", {"entities" : qUnion([Q0]), "oppositeDirection" : true, "depth" : 600 * mm, "hasSecondDirection" : true, "secondDirectionOppositeDirection" : true, "secondDirectionDepth" : 50 * mm});
        }
        {
            var Q0;
            Q0=makeQuery(id+"F1.opExtrude","SWEPT_FACE",FACE,{"disambiguationData":[OSD([sQuery(id+"F0.wireOp",EDGE,"E11.left")])]});
            var sketch = newSketch(context, id + "F10", { "sketchPlane" : qUnion([Q0])});
            skLineSegment(sketch, "E75.bottom", {"start": v(150, -600) * mm, "end": v(-2090, -600) * mm});
            skLineSegment(sketch, "E75.top", {"start": v(150, 2400) * mm, "end": v(-2090, 2400) * mm});
            skLineSegment(sketch, "E75.left", {"start": v(150, -600) * mm, "end": v(150, 2400) * mm});
            skLineSegment(sketch, "E75.right", {"start": v(-2090, -600) * mm, "end": v(-2090, 2400) * mm});
            skLineSegment(sketch, "E76", {"start": v(-2090, 1700) * mm, "end": v(150, 1700) * mm});
            skLineSegment(sketch, "E77", {"start": v(-2090, 1000) * mm, "end": v(150, 1000) * mm});
            skLineSegment(sketch, "E78", {"start": v(-2090, 400) * mm, "end": v(150, 400) * mm});
            skLineSegment(sketch, "E79.bottom", {"start": v(-911.85, 1000) * mm, "end": v(-430.11, 1000) * mm});
            skLineSegment(sketch, "E79.top", {"start": v(-911.85, 400) * mm, "end": v(-430.11, 400) * mm});
            skLineSegment(sketch, "E79.left", {"start": v(-911.85, 1000) * mm, "end": v(-911.85, 400) * mm});
            skLineSegment(sketch, "E79.right", {"start": v(-430.11, 1000) * mm, "end": v(-430.11, 400) * mm});
            skLineSegment(sketch, "E80.bottom", {"start": v(-1565.39, 1000) * mm, "end": v(-1045.38, 1000) * mm});
            skLineSegment(sketch, "E80.top", {"start": v(-1565.39, 400) * mm, "end": v(-1045.38, 400) * mm});
            skLineSegment(sketch, "E80.left", {"start": v(-1565.39, 1000) * mm, "end": v(-1565.39, 400) * mm});
            skLineSegment(sketch, "E80.right", {"start": v(-1045.38, 1000) * mm, "end": v(-1045.38, 400) * mm});
            skLineSegment(sketch, "E81.bottom", {"start": v(-1457.7, 903.22) * mm, "end": v(-1161.3, 903.22) * mm});
            skLineSegment(sketch, "E81.top", {"start": v(-1457.7, 486.62) * mm, "end": v(-1161.3, 486.62) * mm});
            skLineSegment(sketch, "E81.left", {"start": v(-1457.7, 903.22) * mm, "end": v(-1457.7, 486.62) * mm});
            skLineSegment(sketch, "E81.right", {"start": v(-1161.3, 903.22) * mm, "end": v(-1161.3, 486.62) * mm});
            skLineSegment(sketch, "E82.bottom", {"start": v(-777.96, 892.58) * mm, "end": v(-507.08, 892.58) * mm});
            skLineSegment(sketch, "E82.top", {"start": v(-777.96, 468.78) * mm, "end": v(-507.08, 468.78) * mm});
            skLineSegment(sketch, "E82.left", {"start": v(-777.96, 892.58) * mm, "end": v(-777.96, 468.78) * mm});
            skLineSegment(sketch, "E82.right", {"start": v(-507.08, 892.58) * mm, "end": v(-507.08, 468.78) * mm});
            skLineSegment(sketch, "E83.bottom", {"start": v(-1661.57, 1646.06) * mm, "end": v(101.89, 1646.06) * mm});
            skLineSegment(sketch, "E83.top", {"start": v(-1661.57, 1061.99) * mm, "end": v(101.89, 1061.99) * mm});
            skLineSegment(sketch, "E83.left", {"start": v(-1661.57, 1646.06) * mm, "end": v(-1661.57, 1061.99) * mm});
            skLineSegment(sketch, "E83.right", {"start": v(101.89, 1646.06) * mm, "end": v(101.89, 1061.99) * mm});
            skLineSegment(sketch, "E84.bottom", {"start": v(-1670.76, 2400) * mm, "end": v(95.12, 2400) * mm});
            skLineSegment(sketch, "E84.top", {"start": v(-1670.76, 1756.87) * mm, "end": v(95.12, 1756.87) * mm});
            skLineSegment(sketch, "E84.left", {"start": v(-1670.76, 2400) * mm, "end": v(-1670.76, 1756.87) * mm});
            skLineSegment(sketch, "E84.right", {"start": v(95.12, 2400) * mm, "end": v(95.12, 1756.87) * mm});
            skLineSegment(sketch, "E85.bottom", {"start": v(-1370, -600) * mm, "end": v(-1370, -600) * mm});
            skLineSegment(sketch, "E85.top", {"start": v(-1370, 0) * mm, "end": v(-1370, 0) * mm});
            skLineSegment(sketch, "E85.left", {"start": v(-1370, -600) * mm, "end": v(-1370, 0) * mm});
            skLineSegment(sketch, "E85.right", {"start": v(-1370, -600) * mm, "end": v(-1370, 0) * mm});
            skLineSegment(sketch, "E86.bottom", {"start": v(-745.27, 0) * mm, "end": v(-1370, 0) * mm});
            skLineSegment(sketch, "E86.top", {"start": v(-745.27, -600) * mm, "end": v(-1370, -600) * mm});
            skLineSegment(sketch, "E86.left", {"start": v(-745.27, 0) * mm, "end": v(-745.27, -600) * mm});
            skLineSegment(sketch, "E86.right", {"start": v(-1370, 0) * mm, "end": v(-1370, -600) * mm});
            skSolve(sketch);
        }
        {
            var Q0;
            {var subQ0=sQuery(id+"F10.wireOp",EDGE,"E78");Q0=makeQuery(id+"F10.imprint","IMPRINT",FACE,{"disambiguationData":[TD([[makeQuery(id+"F10.imprint","IMPRINT",EDGE,{"derivedFrom":subQ0}),-1.0]])]});}
            var Q1;
            {var subQ0=sQuery(id+"F10.wireOp",EDGE,"E77");Q1=makeQuery(id+"F10.imprint","IMPRINT",FACE,{"disambiguationData":[TD([[makeQuery(id+"F10.imprint","IMPRINT",EDGE,{"derivedFrom":subQ0}),-1.0]])]});}
            var Q2;
            {var subQ0=sQuery(id+"F10.wireOp",EDGE,"E76");Q2=makeQuery(id+"F10.imprint","IMPRINT",FACE,{"disambiguationData":[TD([[makeQuery(id+"F10.imprint","IMPRINT",EDGE,{"derivedFrom":subQ0}),-1.0]])]});}
            var Q3;
            {var subQ0=sQuery(id+"F10.wireOp",EDGE,"E75.top");Q3=makeQuery(id+"F10.imprint","IMPRINT",FACE,{"disambiguationData":[TD([[makeQuery(id+"F10.imprint","IMPRINT",EDGE,{"derivedFrom":subQ0}),1.0]])]});}
            var Q4;
            {var subQ1=sQuery(id+"F0.wireOp",EDGE,"E11.left");var subQ5=makeQuery(id+"F1.opExtrude","CAP_EDGE",EDGE,{"disambiguationData":[OSD([subQ1])],"isStart":true});Q4=makeQuery(id+"F10.imprint","IMPRINT",FACE,{"disambiguationData":[TD([[makeQuery(id+"F10.imprint","IMPRINT",EDGE,{"derivedFrom":subQ5}),1.0]])]});}
            extrude(context, id + "F11", {"entities" : qUnion([Q0, Q1, Q2, Q3, Q4]), "depth" : 600 * mm});
        }
    });
